# Revit family: Strebe 45° VA
name_source: partatom
category: HLS-Bauteile
revit_build: Autodesk Revit 2017 (Build: 20190507_1515(x64)
units: mm (PartAtom-declared; Revit-internal decimal feet)

## family parameters
Arbeitsebenenbasiert = Ja
Beim Laden mit Abzugskörper schneiden = Nein
Bemaßung runder Anschluss = Durchmesser verwenden
Gemeinsam genutzt = Ja
Immer vertikal = Nein
Raumberechnungspunkt = Nein
Teiletyp = Normal

## types (2) — shared parameters
Breite Material = 35 mm
Fabrikat = MEFA
Firma = MEFA Befestigungs- und Montagesysteme GmbH
Gewicht = 0.68 kg
Gewicht pro Bauteil = 0.68 kg
Konsolentyp = 35 + 45
Kurztext2 = L= 301.5 mm für Konsole 35 + 45
Lochdurchmesser = 13 mm
Länge = 302 mm
Material = Edelstahl
Mengeneinheit = St
Vorgabe-Ansicht = 1219 mm
vpe = 1 St

## per-type parameters (varying)
| type | Artikelnummer | EAN | Materialname |
| Strebe 45° V2A | 0480510 | 4250928412706 | V2A |
| Strebe 45° V4A | 0481510 | 4250928413024 | V4A |

note: column(s) folded — value = type name in every type: Kurztext1
